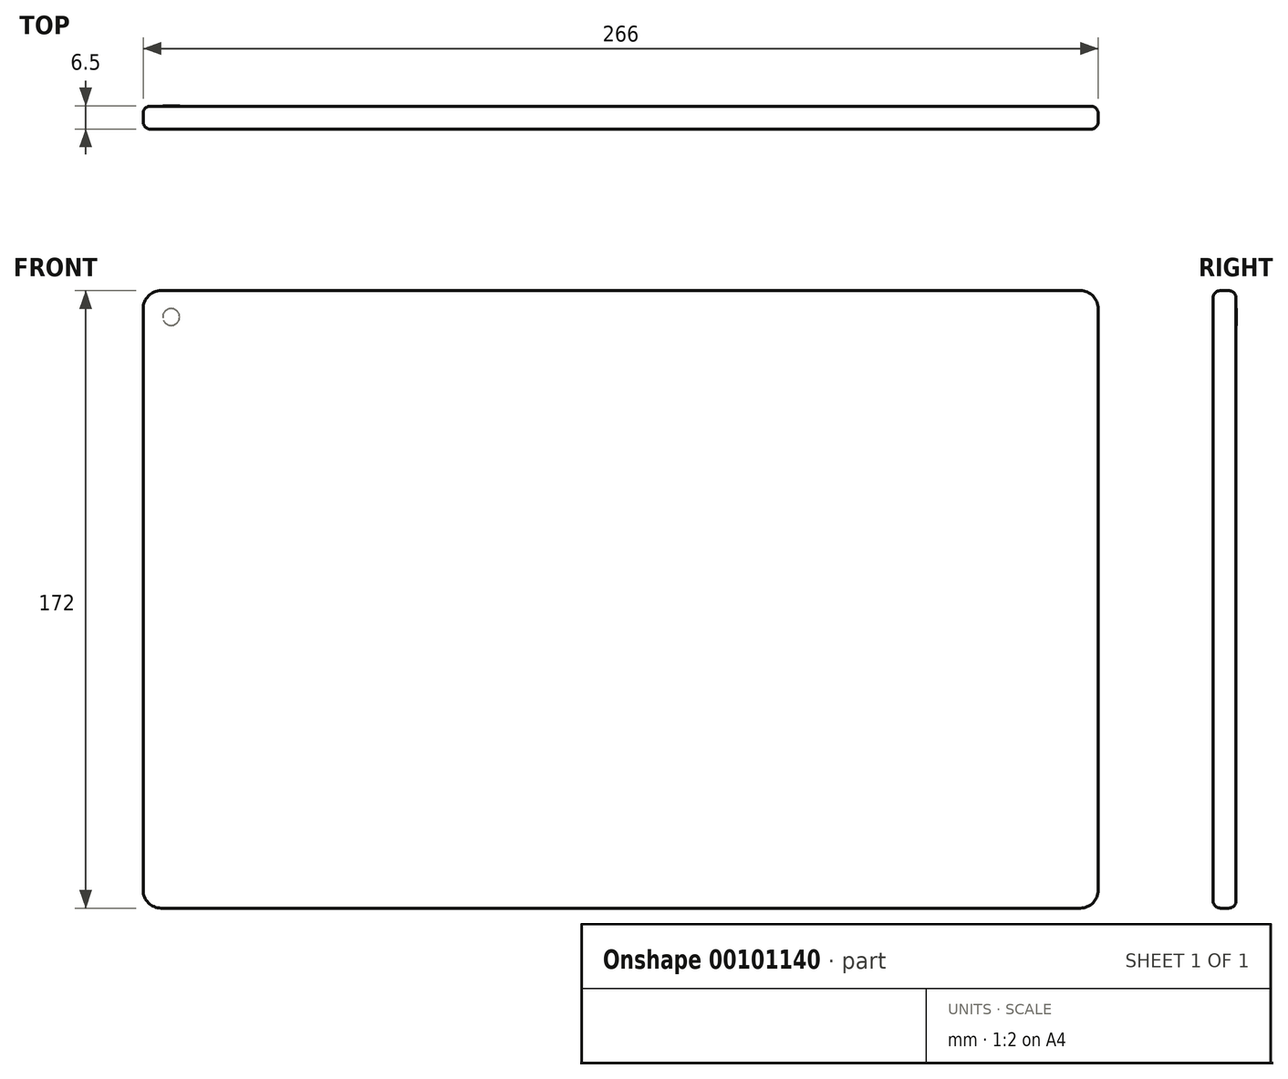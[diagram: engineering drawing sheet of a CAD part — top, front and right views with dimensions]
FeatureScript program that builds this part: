
annotation { "Feature Type Name" : "Feature", "Feature Type Description" : "" }
export const myFeature = defineFeature(function(context is Context, id is Id, definition is map)
    precondition{}
    {
        {
            var Q0;
            Q0=qCreatedBy(makeId("Front.planeOp"),FACE);
            var sketch = newSketch(context, id + "F0", { "sketchPlane" : qUnion([Q0])});
            skLineSegment(sketch, "E0.bottom", {"start": v(-125.66, 95.14) * mm, "end": v(140.34, 95.14) * mm});
            skLineSegment(sketch, "E0.top", {"start": v(-125.66, -76.86) * mm, "end": v(140.34, -76.86) * mm});
            skLineSegment(sketch, "E0.left", {"start": v(-125.66, 95.14) * mm, "end": v(-125.66, -76.86) * mm});
            skLineSegment(sketch, "E0.right", {"start": v(140.34, 95.14) * mm, "end": v(140.34, -76.86) * mm});
            skSolve(sketch);
        }
        {
            var Q0;
            Q0 = qSketchRegion(id + "F0", true);
            extrude(context, id + "F1", {"entities" : qUnion([Q0]), "endBound" : BoundingType.SYMMETRIC, "depth" : 6.4 * mm});
        }
        {
            var Q0;
            Q0=makeQuery(id+"F1.opExtrude","SWEPT_EDGE",EDGE,{"disambiguationData":[OSD([sQuery(id+"F0.wireOp",EDGE,"E0.bottom"),sQuery(id+"F0.wireOp",EDGE,"E0.left")])]});
            var Q1;
            Q1=makeQuery(id+"F1.opExtrude","SWEPT_EDGE",EDGE,{"disambiguationData":[OSD([sQuery(id+"F0.wireOp",EDGE,"E0.bottom"),sQuery(id+"F0.wireOp",EDGE,"E0.right")])]});
            var Q2;
            Q2=makeQuery(id+"F1.opExtrude","SWEPT_EDGE",EDGE,{"disambiguationData":[OSD([sQuery(id+"F0.wireOp",EDGE,"E0.top"),sQuery(id+"F0.wireOp",EDGE,"E0.right")])]});
            var Q3;
            Q3=makeQuery(id+"F1.opExtrude","SWEPT_EDGE",EDGE,{"disambiguationData":[OSD([sQuery(id+"F0.wireOp",EDGE,"E0.top"),sQuery(id+"F0.wireOp",EDGE,"E0.left")])]});
            fillet(context, id + "F2", {"entities" : qUnion([Q0, Q1, Q2, Q3]), "radius" : 5 * mm, "tangentPropagation" : true, "allowEdgeOverflow" : false});
        }
        {
            var Q0;
            Q0=makeQuery(id+"F1.opExtrude","CAP_EDGE",EDGE,{"disambiguationData":[OSD([sQuery(id+"F0.wireOp",EDGE,"E0.top")])],"isStart":true});
            var Q1;
            Q1=makeQuery(id+"F1.opExtrude","CAP_EDGE",EDGE,{"disambiguationData":[OSD([sQuery(id+"F0.wireOp",EDGE,"E0.top")])],"isStart":false});
            var Q2;
            Q2=makeQuery(id+"F1.opExtrude","CAP_EDGE",EDGE,{"disambiguationData":[OSD([sQuery(id+"F0.wireOp",EDGE,"E0.left")])],"isStart":true});
            var Q3;
            Q3=makeQuery(id+"F1.opExtrude","CAP_EDGE",EDGE,{"disambiguationData":[OSD([sQuery(id+"F0.wireOp",EDGE,"E0.left")])],"isStart":false});
            var Q4;
            Q4=makeQuery(id+"F1.opExtrude","CAP_EDGE",EDGE,{"disambiguationData":[OSD([sQuery(id+"F0.wireOp",EDGE,"E0.bottom")])],"isStart":true});
            var Q5;
            Q5=makeQuery(id+"F1.opExtrude","CAP_EDGE",EDGE,{"disambiguationData":[OSD([sQuery(id+"F0.wireOp",EDGE,"E0.right")])],"isStart":true});
            var Q6;
            Q6=makeQuery(id+"F1.opExtrude","CAP_EDGE",EDGE,{"disambiguationData":[OSD([sQuery(id+"F0.wireOp",EDGE,"E0.right")])],"isStart":false});
            var Q7;
            Q7=makeQuery(id+"F1.opExtrude","CAP_EDGE",EDGE,{"disambiguationData":[OSD([sQuery(id+"F0.wireOp",EDGE,"E0.bottom")])],"isStart":false});
            var Q8;
            {var subQ0=sQuery(id+"F0.wireOp",EDGE,"E0.left");var subQ1=sQuery(id+"F0.wireOp",EDGE,"E0.top");Q8=makeQuery(id+"F2.opFillet","BLEND_EDGE",EDGE,{"blendedFrom":[makeQuery(id+"F1.opExtrude","SWEPT_EDGE",EDGE,{"disambiguationData":[OSD([subQ1,subQ0])]}),makeQuery(id+"F1.opExtrude","CAP_FACE",FACE,{"disambiguationData":[OSD([sQuery(id+"F0.wireOp",EDGE,"E0.bottom"),subQ1,subQ0,sQuery(id+"F0.wireOp",EDGE,"E0.right")])],"isStart":false})],"blendedInto":[makeQuery(id+"F1.opExtrude","CAP_FACE",FACE,{"disambiguationData":[OSD([sQuery(id+"F0.wireOp",EDGE,"E0.bottom"),subQ1,subQ0,sQuery(id+"F0.wireOp",EDGE,"E0.right")])],"isStart":false})]});}
            var Q9;
            {var subQ0=sQuery(id+"F0.wireOp",EDGE,"E0.left");var subQ1=sQuery(id+"F0.wireOp",EDGE,"E0.top");Q9=makeQuery(id+"F2.opFillet","BLEND_EDGE",EDGE,{"blendedFrom":[makeQuery(id+"F1.opExtrude","SWEPT_EDGE",EDGE,{"disambiguationData":[OSD([subQ1,subQ0])]}),makeQuery(id+"F1.opExtrude","CAP_FACE",FACE,{"disambiguationData":[OSD([sQuery(id+"F0.wireOp",EDGE,"E0.bottom"),subQ1,subQ0,sQuery(id+"F0.wireOp",EDGE,"E0.right")])],"isStart":true})],"blendedInto":[makeQuery(id+"F1.opExtrude","CAP_FACE",FACE,{"disambiguationData":[OSD([sQuery(id+"F0.wireOp",EDGE,"E0.bottom"),subQ1,subQ0,sQuery(id+"F0.wireOp",EDGE,"E0.right")])],"isStart":true})]});}
            var Q10;
            {var subQ0=sQuery(id+"F0.wireOp",EDGE,"E0.left");var subQ1=sQuery(id+"F0.wireOp",EDGE,"E0.bottom");Q10=makeQuery(id+"F2.opFillet","BLEND_EDGE",EDGE,{"blendedFrom":[makeQuery(id+"F1.opExtrude","SWEPT_EDGE",EDGE,{"disambiguationData":[OSD([subQ1,subQ0])]}),makeQuery(id+"F1.opExtrude","CAP_FACE",FACE,{"disambiguationData":[OSD([subQ1,sQuery(id+"F0.wireOp",EDGE,"E0.top"),subQ0,sQuery(id+"F0.wireOp",EDGE,"E0.right")])],"isStart":false})],"blendedInto":[makeQuery(id+"F1.opExtrude","CAP_FACE",FACE,{"disambiguationData":[OSD([subQ1,sQuery(id+"F0.wireOp",EDGE,"E0.top"),subQ0,sQuery(id+"F0.wireOp",EDGE,"E0.right")])],"isStart":false})]});}
            var Q11;
            {var subQ0=sQuery(id+"F0.wireOp",EDGE,"E0.left");var subQ1=sQuery(id+"F0.wireOp",EDGE,"E0.bottom");Q11=makeQuery(id+"F2.opFillet","BLEND_EDGE",EDGE,{"blendedFrom":[makeQuery(id+"F1.opExtrude","SWEPT_EDGE",EDGE,{"disambiguationData":[OSD([subQ1,subQ0])]}),makeQuery(id+"F1.opExtrude","CAP_FACE",FACE,{"disambiguationData":[OSD([subQ1,sQuery(id+"F0.wireOp",EDGE,"E0.top"),subQ0,sQuery(id+"F0.wireOp",EDGE,"E0.right")])],"isStart":true})],"blendedInto":[makeQuery(id+"F1.opExtrude","CAP_FACE",FACE,{"disambiguationData":[OSD([subQ1,sQuery(id+"F0.wireOp",EDGE,"E0.top"),subQ0,sQuery(id+"F0.wireOp",EDGE,"E0.right")])],"isStart":true})]});}
            var Q12;
            {var subQ0=sQuery(id+"F0.wireOp",EDGE,"E0.right");var subQ1=sQuery(id+"F0.wireOp",EDGE,"E0.bottom");Q12=makeQuery(id+"F2.opFillet","BLEND_EDGE",EDGE,{"blendedFrom":[makeQuery(id+"F1.opExtrude","SWEPT_EDGE",EDGE,{"disambiguationData":[OSD([subQ1,subQ0])]}),makeQuery(id+"F1.opExtrude","CAP_FACE",FACE,{"disambiguationData":[OSD([subQ1,sQuery(id+"F0.wireOp",EDGE,"E0.top"),sQuery(id+"F0.wireOp",EDGE,"E0.left"),subQ0])],"isStart":false})],"blendedInto":[makeQuery(id+"F1.opExtrude","CAP_FACE",FACE,{"disambiguationData":[OSD([subQ1,sQuery(id+"F0.wireOp",EDGE,"E0.top"),sQuery(id+"F0.wireOp",EDGE,"E0.left"),subQ0])],"isStart":false})]});}
            var Q13;
            {var subQ0=sQuery(id+"F0.wireOp",EDGE,"E0.right");var subQ1=sQuery(id+"F0.wireOp",EDGE,"E0.top");Q13=makeQuery(id+"F2.opFillet","BLEND_EDGE",EDGE,{"blendedFrom":[makeQuery(id+"F1.opExtrude","SWEPT_EDGE",EDGE,{"disambiguationData":[OSD([subQ1,subQ0])]}),makeQuery(id+"F1.opExtrude","CAP_FACE",FACE,{"disambiguationData":[OSD([sQuery(id+"F0.wireOp",EDGE,"E0.bottom"),subQ1,sQuery(id+"F0.wireOp",EDGE,"E0.left"),subQ0])],"isStart":true})],"blendedInto":[makeQuery(id+"F1.opExtrude","CAP_FACE",FACE,{"disambiguationData":[OSD([sQuery(id+"F0.wireOp",EDGE,"E0.bottom"),subQ1,sQuery(id+"F0.wireOp",EDGE,"E0.left"),subQ0])],"isStart":true})]});}
            var Q14;
            {var subQ0=sQuery(id+"F0.wireOp",EDGE,"E0.right");var subQ1=sQuery(id+"F0.wireOp",EDGE,"E0.top");Q14=makeQuery(id+"F2.opFillet","BLEND_EDGE",EDGE,{"blendedFrom":[makeQuery(id+"F1.opExtrude","SWEPT_EDGE",EDGE,{"disambiguationData":[OSD([subQ1,subQ0])]}),makeQuery(id+"F1.opExtrude","CAP_FACE",FACE,{"disambiguationData":[OSD([sQuery(id+"F0.wireOp",EDGE,"E0.bottom"),subQ1,sQuery(id+"F0.wireOp",EDGE,"E0.left"),subQ0])],"isStart":false})],"blendedInto":[makeQuery(id+"F1.opExtrude","CAP_FACE",FACE,{"disambiguationData":[OSD([sQuery(id+"F0.wireOp",EDGE,"E0.bottom"),subQ1,sQuery(id+"F0.wireOp",EDGE,"E0.left"),subQ0])],"isStart":false})]});}
            var Q15;
            {var subQ0=sQuery(id+"F0.wireOp",EDGE,"E0.right");var subQ1=sQuery(id+"F0.wireOp",EDGE,"E0.bottom");Q15=makeQuery(id+"F2.opFillet","BLEND_EDGE",EDGE,{"blendedFrom":[makeQuery(id+"F1.opExtrude","SWEPT_EDGE",EDGE,{"disambiguationData":[OSD([subQ1,subQ0])]}),makeQuery(id+"F1.opExtrude","CAP_FACE",FACE,{"disambiguationData":[OSD([subQ1,sQuery(id+"F0.wireOp",EDGE,"E0.top"),sQuery(id+"F0.wireOp",EDGE,"E0.left"),subQ0])],"isStart":true})],"blendedInto":[makeQuery(id+"F1.opExtrude","CAP_FACE",FACE,{"disambiguationData":[OSD([subQ1,sQuery(id+"F0.wireOp",EDGE,"E0.top"),sQuery(id+"F0.wireOp",EDGE,"E0.left"),subQ0])],"isStart":true})]});}
            fillet(context, id + "F3", {"entities" : qUnion([Q0, Q1, Q2, Q3, Q4, Q5, Q6, Q7, Q8, Q9, Q10, Q11, Q12, Q13, Q14, Q15]), "radius" : 2 * mm, "tangentPropagation" : true, "allowEdgeOverflow" : false});
        }
        {
            var Q0;
            Q0=makeQuery(id+"F1.opExtrude","CAP_FACE",FACE,{"disambiguationData":[OSD([sQuery(id+"F0.wireOp",EDGE,"E0.bottom"),sQuery(id+"F0.wireOp",EDGE,"E0.top"),sQuery(id+"F0.wireOp",EDGE,"E0.left"),sQuery(id+"F0.wireOp",EDGE,"E0.right")])],"isStart":true});
            var sketch = newSketch(context, id + "F4", { "sketchPlane" : qUnion([Q0])});
            skCircle(sketch, "E1", {"center": v(117.85, 87.8) * mm, "radius": 2.35 * mm});
            skSolve(sketch);
        }
        {
            var Q0;
            Q0=makeQuery(id+"F4.imprint","IMPRINT",FACE,{"disambiguationData":[TD([[makeQuery(id+"F4.imprint","IMPRINT",EDGE,{"derivedFrom":sQuery(id+"F4.wireOp",EDGE,"E1")}),1.0]])]});
            extrude(context, id + "F5", {"entities" : qUnion([Q0]), "operationType" : NewBodyOperationType.ADD, "depth" : 0.1 * mm});
        }
    });
